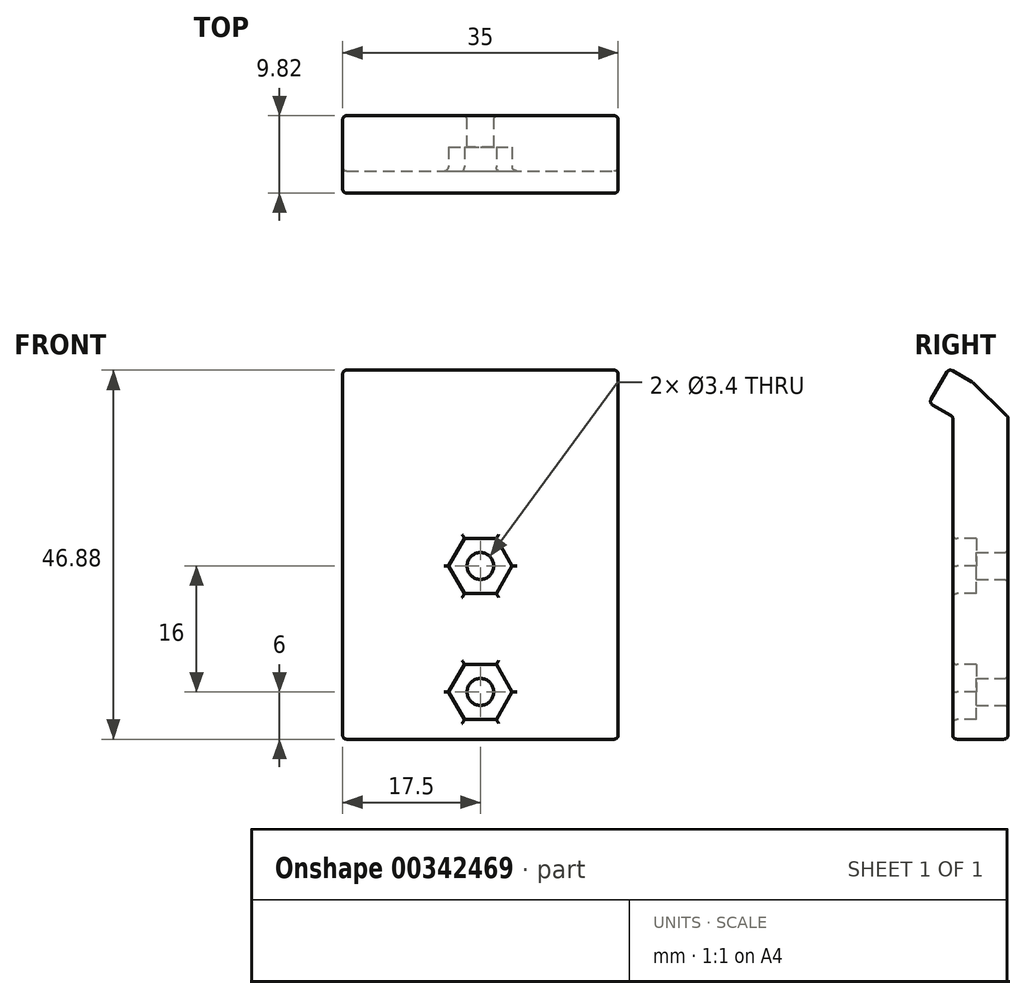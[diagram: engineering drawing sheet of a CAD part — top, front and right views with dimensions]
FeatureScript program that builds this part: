
annotation { "Feature Type Name" : "Feature", "Feature Type Description" : "" }
export const myFeature = defineFeature(function(context is Context, id is Id, definition is map)
    precondition{}
    {
        {
            var Q0;
            Q0=qCreatedBy(makeId("Front.planeOp"),FACE);
            var sketch = newSketch(context, id + "F0", { "sketchPlane" : qUnion([Q0])});
            skLineSegment(sketch, "E0.bottom", {"start": v(-17.5, 0) * mm, "end": v(17.5, 0) * mm});
            skLineSegment(sketch, "E0.top", {"start": v(-17.5, 41) * mm, "end": v(17.5, 41) * mm});
            skLineSegment(sketch, "E0.left", {"start": v(-17.5, 0) * mm, "end": v(-17.5, 41) * mm});
            skLineSegment(sketch, "E0.right", {"start": v(17.5, 0) * mm, "end": v(17.5, 41) * mm});
            skCircle(sketch, "E1", {"center": v(0, 6) * mm, "radius": 1.7 * mm});
            skCircle(sketch, "E2", {"center": v(0, 22) * mm, "radius": 1.7 * mm});
            skSolve(sketch);
        }
        {
            var Q0;
            Q0=makeQuery(id+"F0.imprint","IMPRINT",FACE,{"disambiguationData":[TD([[makeQuery(id+"F0.imprint","IMPRINT",EDGE,{"derivedFrom":sQuery(id+"F0.wireOp",EDGE,"E0.bottom")}),1.0]])]});
            extrude(context, id + "F1", {"entities" : qUnion([Q0]), "depth" : 7 * mm});
        }
        {
            var Q0;
            Q0=makeQuery(id+"F1.opExtrude","SWEPT_FACE",FACE,{"disambiguationData":[OSD([sQuery(id+"F0.wireOp",EDGE,"E0.right")])]});
            var sketch = newSketch(context, id + "F2", { "sketchPlane" : qUnion([Q0])});
            skLineSegment(sketch, "E3", {"start": v(-7, 41) * mm, "end": v(-10, 42.73) * mm});
            skLineSegment(sketch, "E4", {"start": v(-10, 42.73) * mm, "end": v(-7.5, 47.06) * mm});
            skLineSegment(sketch, "E5", {"start": v(-7.5, 47.06) * mm, "end": v(-4.5, 45.33) * mm});
            skLineSegment(sketch, "E6", {"start": v(-7, 41) * mm, "end": v(-4.5, 45.33) * mm, "construction": true});
            skLineSegment(sketch, "E7", {"start": v(-4.5, 45.33) * mm, "end": v(0, 41) * mm});
            skSolve(sketch);
        }
        {
            var Q0;
            Q0=makeQuery(id+"F2.imprint","IMPRINT",FACE,{"disambiguationData":[TD([[makeQuery(id+"F2.imprint","IMPRINT",EDGE,{"derivedFrom":sQuery(id+"F2.wireOp",EDGE,"E3")}),-1.0]])]});
            var Q1;
            Q1=makeQuery(id+"F1.opExtrude","SWEPT_FACE",FACE,{"disambiguationData":[OSD([sQuery(id+"F0.wireOp",EDGE,"E0.left")])]});
            extrude(context, id + "F3", {"entities" : qUnion([Q0]), "operationType" : NewBodyOperationType.ADD, "endBound" : BoundingType.UP_TO_SURFACE, "oppositeDirection" : true, "endBoundEntityFace" : qUnion([Q1]), "depth" : 25 * mm});
        }
        {
            var Q0;
            Q0=makeQuery(id+"F1.opExtrude","CAP_FACE",FACE,{"disambiguationData":[OSD([sQuery(id+"F0.wireOp",EDGE,"E0.bottom"),sQuery(id+"F0.wireOp",EDGE,"E0.top"),sQuery(id+"F0.wireOp",EDGE,"E0.left"),sQuery(id+"F0.wireOp",EDGE,"E0.right"),sQuery(id+"F0.wireOp",EDGE,"E1"),sQuery(id+"F0.wireOp",EDGE,"E2")])],"isStart":false});
            var sketch = newSketch(context, id + "F4", { "sketchPlane" : qUnion([Q0])});
            skCircle(sketch, "E8.cCircle", {"center": v(0, 22) * mm, "radius": 3.5 * mm, "construction": true});
            skLineSegment(sketch, "E8.0", {"start": v(2.02, 25.5) * mm, "end": v(4.04, 22) * mm});
            skLineSegment(sketch, "E8.1", {"start": v(4.04, 22) * mm, "end": v(2.02, 18.5) * mm});
            skLineSegment(sketch, "E8.2", {"start": v(2.02, 18.5) * mm, "end": v(-2.02, 18.5) * mm});
            skLineSegment(sketch, "E8.3", {"start": v(-2.02, 18.5) * mm, "end": v(-4.04, 22) * mm});
            skLineSegment(sketch, "E8.4", {"start": v(-4.04, 22) * mm, "end": v(-2.02, 25.5) * mm});
            skLineSegment(sketch, "E8.5", {"start": v(-2.02, 25.5) * mm, "end": v(2.02, 25.5) * mm});
            skPoint(sketch, "E8.0.midPoint", {"position": v(3.03, 23.75) * mm});
            skCircle(sketch, "E9.cCircle", {"center": v(0, 6) * mm, "radius": 3.5 * mm, "construction": true});
            skLineSegment(sketch, "E9.0", {"start": v(2.02, 9.5) * mm, "end": v(4.04, 6) * mm});
            skLineSegment(sketch, "E9.1", {"start": v(4.04, 6) * mm, "end": v(2.02, 2.5) * mm});
            skLineSegment(sketch, "E9.2", {"start": v(2.02, 2.5) * mm, "end": v(-2.02, 2.5) * mm});
            skLineSegment(sketch, "E9.3", {"start": v(-2.02, 2.5) * mm, "end": v(-4.04, 6) * mm});
            skLineSegment(sketch, "E9.4", {"start": v(-4.04, 6) * mm, "end": v(-2.02, 9.5) * mm});
            skLineSegment(sketch, "E9.5", {"start": v(-2.02, 9.5) * mm, "end": v(2.02, 9.5) * mm});
            skPoint(sketch, "E9.0.midPoint", {"position": v(3.03, 7.75) * mm});
            skSolve(sketch);
        }
        {
            var Q0;
            Q0=makeQuery(id+"F4.imprint","IMPRINT",FACE,{"disambiguationData":[TD([[makeQuery(id+"F4.imprint","IMPRINT",EDGE,{"derivedFrom":sQuery(id+"F4.wireOp",EDGE,"E8.0")}),-1.0]])]});
            var Q1;
            Q1=makeQuery(id+"F4.imprint","IMPRINT",FACE,{"disambiguationData":[TD([[makeQuery(id+"F4.imprint","IMPRINT",EDGE,{"derivedFrom":sQuery(id+"F4.wireOp",EDGE,"E9.0")}),-1.0]])]});
            extrude(context, id + "F5", {"entities" : qUnion([Q0, Q1]), "operationType" : NewBodyOperationType.REMOVE, "oppositeDirection" : true, "depth" : 3 * mm});
        }
        {
            var Q0;
            {var subQ0=sQuery(id+"F0.wireOp",EDGE,"E0.right");Q0=makeQuery(id+"F3.boolean.opBoolean","MERGE",FACE,{"derivedFrom":[makeQuery(id+"F1.opExtrude","SWEPT_FACE",FACE,{"disambiguationData":[OSD([subQ0])]}),makeQuery(id+"F3.opExtrude","CAP_FACE",FACE,{"disambiguationData":[OSD([sQuery(id+"F0.wireOp",EDGE,"E0.top"),subQ0,sQuery(id+"F2.wireOp",EDGE,"E3"),sQuery(id+"F2.wireOp",EDGE,"E4"),sQuery(id+"F2.wireOp",EDGE,"E5"),sQuery(id+"F2.wireOp",EDGE,"E7")])],"isStart":true})]});}
            var Q1;
            Q1=makeQuery(id+"F1.opExtrude","CAP_FACE",FACE,{"disambiguationData":[OSD([sQuery(id+"F0.wireOp",EDGE,"E0.bottom"),sQuery(id+"F0.wireOp",EDGE,"E0.top"),sQuery(id+"F0.wireOp",EDGE,"E0.left"),sQuery(id+"F0.wireOp",EDGE,"E0.right"),sQuery(id+"F0.wireOp",EDGE,"E1"),sQuery(id+"F0.wireOp",EDGE,"E2")])],"isStart":false});
            var Q2;
            Q2=makeQuery(id+"F3.opExtrude","SWEPT_FACE",FACE,{"disambiguationData":[OSD([sQuery(id+"F2.wireOp",EDGE,"E4")])]});
            var Q3;
            {var subQ0=sQuery(id+"F0.wireOp",EDGE,"E0.left");Q3=makeQuery(id+"F3.boolean.opBoolean","MERGE",FACE,{"derivedFrom":[makeQuery(id+"F1.opExtrude","SWEPT_FACE",FACE,{"disambiguationData":[OSD([subQ0])]}),makeQuery(id+"F3.opExtrude","CAP_FACE",FACE,{"disambiguationData":[OSD([subQ0])],"isStart":false})]});}
            var Q4;
            Q4=makeQuery(id+"F1.opExtrude","CAP_FACE",FACE,{"disambiguationData":[OSD([sQuery(id+"F0.wireOp",EDGE,"E0.bottom"),sQuery(id+"F0.wireOp",EDGE,"E0.top"),sQuery(id+"F0.wireOp",EDGE,"E0.left"),sQuery(id+"F0.wireOp",EDGE,"E0.right"),sQuery(id+"F0.wireOp",EDGE,"E1"),sQuery(id+"F0.wireOp",EDGE,"E2")])],"isStart":true});
            var Q5;
            Q5=makeQuery(id+"F3.opExtrude","SWEPT_FACE",FACE,{"disambiguationData":[OSD([sQuery(id+"F2.wireOp",EDGE,"E7")])]});
            fillet(context, id + "F6", {"entities" : qUnion([Q0, Q1, Q2, Q3, Q4, Q5]), "radius" : 0.5 * mm, "tangentPropagation" : true, "allowEdgeOverflow" : false});
        }
    });
